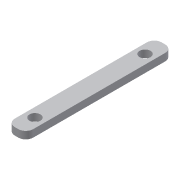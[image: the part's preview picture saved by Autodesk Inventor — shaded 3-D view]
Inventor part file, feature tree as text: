
AUTODESK INVENTOR PART (.ipt)
format: ipt  version: 2013 (Build 170138000, 138)  size: 84,480 bytes
history: native  units: mm
features: hole x2, extrude x1, sketch x1
ambient origin geometry x8: Origin, YZ Plane, XZ Plane, XY Plane, X Axis, Y Axis, Z Axis, Center Point
bodies: Volumenkörper1 (feature_tree)
feature tree (4):
  extrude  "Extrusion1"  [1 undecoded]
  hole  "Bohrung1"  [1 undecoded]
  hole  "Bohrung2"  [1 undecoded]
  sketch  "Skizze1"  dims[d0=5.0mm d1=40.0mm d2=2.0mm d3=2.0mm d4=0.0mm d5=2.5mm d6=5.0mm d7=3.0mm d8=6.0mm d9=4.0mm d10=2.0mm d11=90.0deg d12=8.0mm d13=20.594885mm d14=2.5mm d15=5.0mm d16=3.0mm d17=6.0mm d18=4.0mm d19=2.0mm d20=90.0deg d21=8.0mm d22=20.594885mm]
note: 3 required parameter values undecoded (feature->parameter linkage not recoverable at this tier; creation-order binding heuristic only, values carry confidence <= 0.55)
